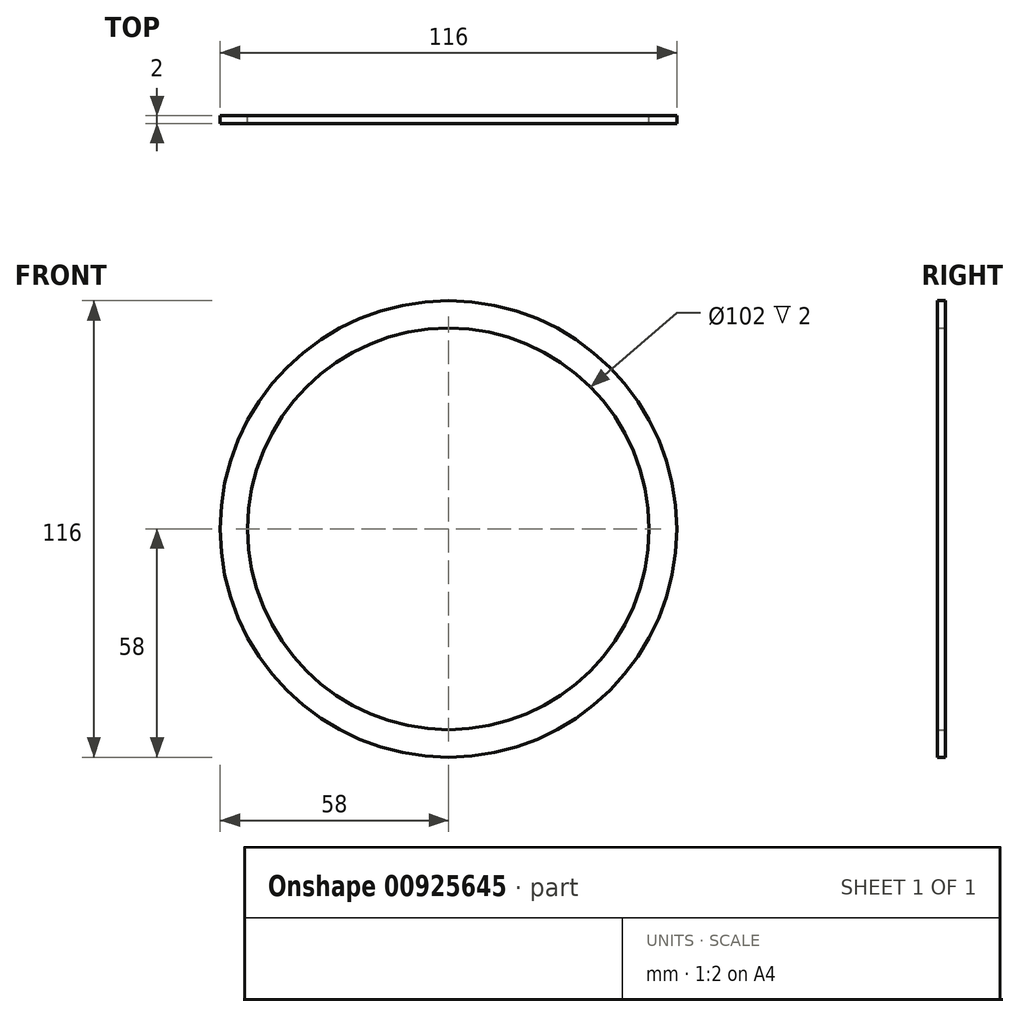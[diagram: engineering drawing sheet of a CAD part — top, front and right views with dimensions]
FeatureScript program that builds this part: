
annotation { "Feature Type Name" : "Feature", "Feature Type Description" : "" }
export const myFeature = defineFeature(function(context is Context, id is Id, definition is map)
    precondition{}
    {
        {
            var Q0;
            Q0=qCreatedBy(makeId("Front.planeOp"),FACE);
            var sketch = newSketch(context, id + "F0", { "sketchPlane" : qUnion([Q0])});
            skCircle(sketch, "E0", {"center": v(0, 0) * mm, "radius": 58 * mm});
            skCircle(sketch, "E1", {"center": v(0, 0) * mm, "radius": 51 * mm});
            skSolve(sketch);
        }
        {
            var Q0;
            Q0=makeQuery(id+"F0.imprint","IMPRINT",FACE,{"disambiguationData":[TD([[makeQuery(id+"F0.imprint","IMPRINT",EDGE,{"derivedFrom":sQuery(id+"F0.wireOp",EDGE,"E0")}),1.0]])]});
            extrude(context, id + "F1", {"entities" : qUnion([Q0]), "depth" : 2 * mm, "offsetDistance" : 25 * mm});
        }
    });
